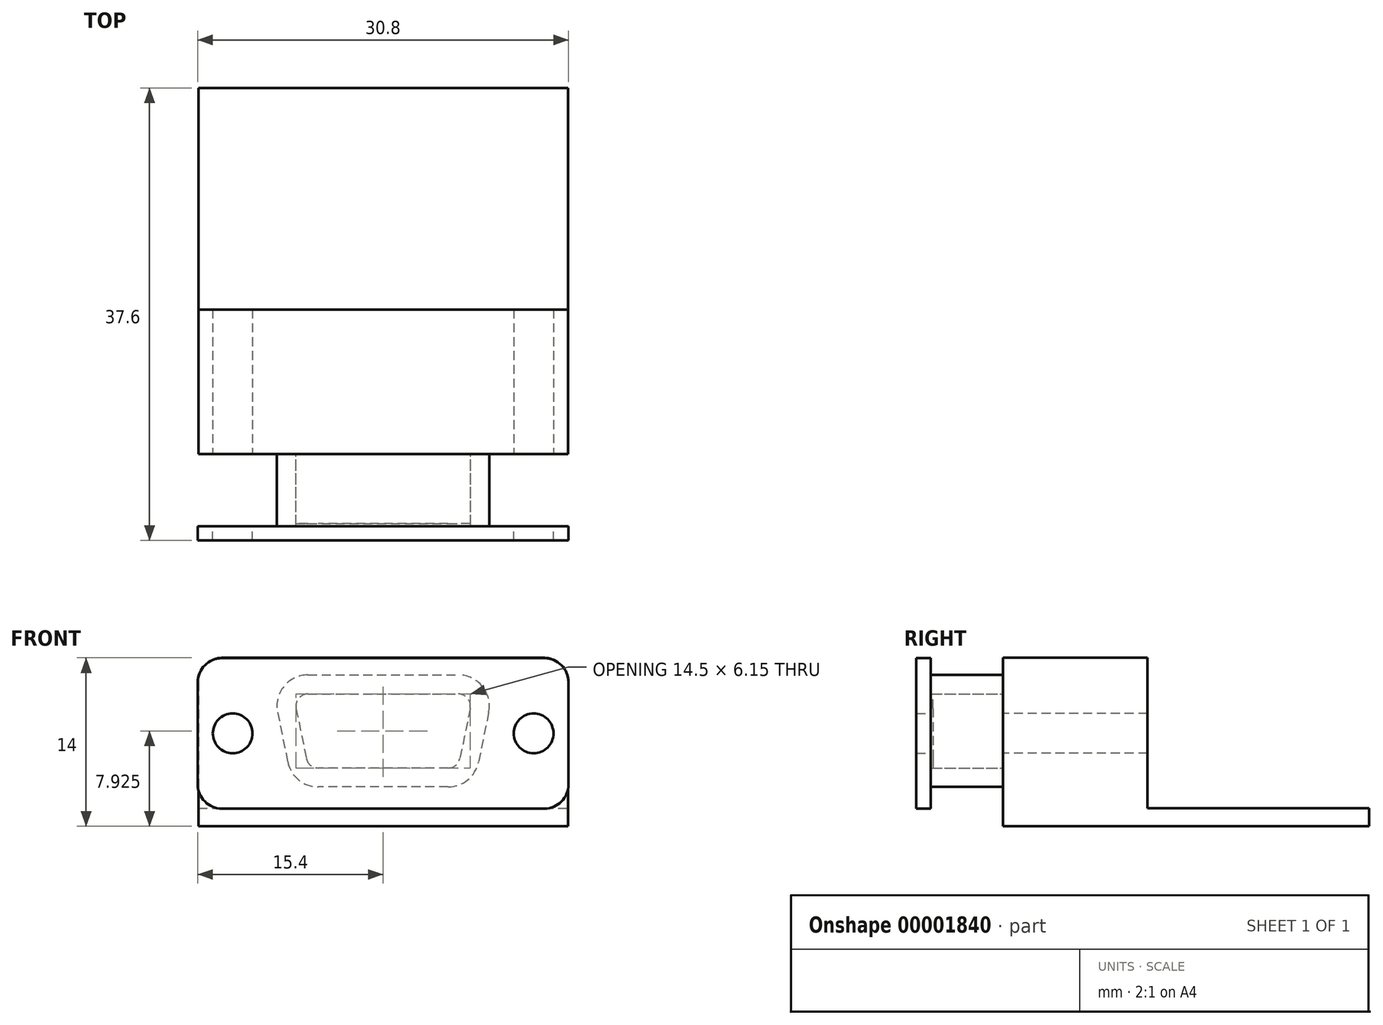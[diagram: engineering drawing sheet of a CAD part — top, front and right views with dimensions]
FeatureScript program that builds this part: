
annotation { "Feature Type Name" : "Feature", "Feature Type Description" : "" }
export const myFeature = defineFeature(function(context is Context, id is Id, definition is map)
    precondition{}
    {
        {
            var Q0;
            Q0=qCreatedBy(makeId("Front.planeOp"),FACE);
            var sketch = newSketch(context, id + "F0", { "sketchPlane" : qUnion([Q0])});
            skLineSegment(sketch, "E0.bottom", {"start": v(-13.35, 14) * mm, "end": v(13.35, 14) * mm});
            skLineSegment(sketch, "E0.top", {"start": v(-15.35, 0) * mm, "end": v(15.35, 0) * mm});
            skLineSegment(sketch, "E0.left", {"start": v(-15.35, 12) * mm, "end": v(-15.35, 0) * mm});
            skLineSegment(sketch, "E0.right", {"start": v(15.35, 12) * mm, "end": v(15.35, 0) * mm});
            skPoint(sketch, "E0.middle", {"position": v(0, 7) * mm});
            skLineSegment(sketch, "E1", {"start": v(-6.25, 11) * mm, "end": v(6.25, 11) * mm});
            skLineSegment(sketch, "E2", {"start": v(7.23, 9.8) * mm, "end": v(6.38, 5.65) * mm});
            skLineSegment(sketch, "E3", {"start": v(5.4, 4.85) * mm, "end": v(-5.4, 4.85) * mm});
            skLineSegment(sketch, "E4", {"start": v(0, 0) * mm, "end": v(0, 7) * mm, "construction": true});
            skLineSegment(sketch, "E5.MirrorCS", {"start": v(-7.23, 9.8) * mm, "end": v(-6.38, 5.65) * mm});
            skPoint(sketch, "E6.visualSharp", {"position": v(-7.48, 11) * mm});
            skArc(sketch, "E6.filletArc", {"start": v(-6.25, 11) * mm, "mid": v(-7.02, 10.63) * mm, "end": v(-7.23, 9.8) * mm});
            skPoint(sketch, "E7.visualSharp", {"position": v(-6.22, 4.85) * mm});
            skArc(sketch, "E7.filletArc", {"start": v(-6.38, 5.65) * mm, "mid": v(-6.03, 5.08) * mm, "end": v(-5.4, 4.85) * mm});
            skPoint(sketch, "E8.visualSharp", {"position": v(6.22, 4.85) * mm});
            skArc(sketch, "E8.filletArc", {"start": v(5.4, 4.85) * mm, "mid": v(6.03, 5.08) * mm, "end": v(6.38, 5.65) * mm});
            skPoint(sketch, "E9.visualSharp", {"position": v(7.48, 11) * mm});
            skArc(sketch, "E9.filletArc", {"start": v(7.23, 9.8) * mm, "mid": v(7.02, 10.63) * mm, "end": v(6.25, 11) * mm});
            skLineSegment(sketch, "E10", {"start": v(-15.35, 1.5) * mm, "end": v(15.35, 1.5) * mm});
            skPoint(sketch, "E11.visualSharp", {"position": v(-15.35, 14) * mm});
            skArc(sketch, "E11.filletArc", {"start": v(-13.35, 14) * mm, "mid": v(-14.76, 13.41) * mm, "end": v(-15.35, 12) * mm});
            skPoint(sketch, "E12.visualSharp", {"position": v(15.35, 14) * mm});
            skArc(sketch, "E12.filletArc", {"start": v(15.35, 12) * mm, "mid": v(14.76, 13.41) * mm, "end": v(13.35, 14) * mm});
            skLineSegment(sketch, "E13", {"start": v(-12.5, 7.72) * mm, "end": v(12.5, 7.72) * mm, "construction": true});
            skLineSegment(sketch, "E14", {"start": v(0, 7) * mm, "end": v(0, 7.72) * mm, "construction": true});
            skPoint(sketch, "E15", {"position": v(-6.8, 7.72) * mm});
            skCircle(sketch, "E16", {"center": v(-12.5, 7.72) * mm, "radius": 1.65 * mm});
            skCircle(sketch, "E17", {"center": v(12.5, 7.72) * mm, "radius": 1.65 * mm});
            skSolve(sketch);
        }
        {
            var Q0;
            {var subQ0=sQuery(id+"F0.wireOp",EDGE,"E0.top");Q0=makeQuery(id+"F0.imprint","IMPRINT",FACE,{"disambiguationData":[TD([[makeQuery(id+"F0.imprint","IMPRINT",EDGE,{"derivedFrom":subQ0}),1.0]])]});}
            extrude(context, id + "F1", {"entities" : qUnion([Q0]), "oppositeDirection" : true, "depth" : 30.4 * mm});
        }
        {
            var Q0;
            Q0=makeQuery(id+"F0.imprint","IMPRINT",FACE,{"disambiguationData":[TD([[makeQuery(id+"F0.imprint","IMPRINT",EDGE,{"derivedFrom":sQuery(id+"F0.wireOp",EDGE,"E0.bottom")}),-1.0]])]});
            var Q1;
            Q1=makeQuery(id+"F0.imprint","IMPRINT",FACE,{"disambiguationData":[TD([[makeQuery(id+"F0.imprint","IMPRINT",EDGE,{"derivedFrom":sQuery(id+"F0.wireOp",EDGE,"E1")}),-1.0]])]});
            extrude(context, id + "F2", {"entities" : qUnion([Q0, Q1]), "operationType" : NewBodyOperationType.ADD, "oppositeDirection" : true, "depth" : 12 * mm});
        }
        {
            var Q0;
            Q0=makeQuery(id+"F0.imprint","IMPRINT",FACE,{"disambiguationData":[TD([[makeQuery(id+"F0.imprint","IMPRINT",EDGE,{"derivedFrom":sQuery(id+"F0.wireOp",EDGE,"E1")}),-1.0]])]});
            extrude(context, id + "F3", {"entities" : qUnion([Q0]), "operationType" : NewBodyOperationType.ADD, "depth" : 5.8 * mm});
        }
        {
            var Q0;
            Q0=makeQuery(id+"F0.imprint","IMPRINT",FACE,{"disambiguationData":[TD([[makeQuery(id+"F0.imprint","IMPRINT",EDGE,{"derivedFrom":sQuery(id+"F0.wireOp",EDGE,"E0.bottom")}),-1.0]])]});
            var sketch = newSketch(context, id + "F4", { "sketchPlane" : qUnion([Q0])});
            skArc(sketch, "E18.0", {"start": v(-6.25, 12.58) * mm, "mid": v(-8.25, 11.63) * mm, "end": v(-8.77, 9.48) * mm});
            skLineSegment(sketch, "E18.1", {"start": v(-8.77, 9.48) * mm, "end": v(-7.92, 5.33) * mm});
            skLineSegment(sketch, "E18.2", {"start": v(-6.25, 12.58) * mm, "end": v(6.25, 12.58) * mm});
            skArc(sketch, "E18.3", {"start": v(-7.92, 5.33) * mm, "mid": v(-7.03, 3.85) * mm, "end": v(-5.4, 3.27) * mm});
            skArc(sketch, "E18.4", {"start": v(8.77, 9.48) * mm, "mid": v(8.25, 11.63) * mm, "end": v(6.25, 12.58) * mm});
            skLineSegment(sketch, "E18.5", {"start": v(8.77, 9.48) * mm, "end": v(7.92, 5.33) * mm});
            skArc(sketch, "E18.6", {"start": v(5.4, 3.28) * mm, "mid": v(7.03, 3.85) * mm, "end": v(7.92, 5.33) * mm});
            skLineSegment(sketch, "E18.7", {"start": v(5.4, 3.28) * mm, "end": v(-5.4, 3.28) * mm});
            skSolve(sketch);
        }
        {
            var Q0;
            Q0=makeQuery(id+"F4.imprint","IMPRINT",FACE,{"disambiguationData":[TD([[makeQuery(id+"F4.imprint","IMPRINT",EDGE,{"derivedFrom":sQuery(id+"F4.wireOp",EDGE,"E18.0")}),1.0]])]});
            extrude(context, id + "F5", {"entities" : qUnion([Q0]), "depth" : 6 * mm});
        }
        {
            var Q0;
            Q0=makeQuery(id+"F5.opExtrude","CAP_FACE",FACE,{"disambiguationData":[OSD([sQuery(id+"F0.wireOp",EDGE,"E1"),sQuery(id+"F0.wireOp",EDGE,"E2"),sQuery(id+"F0.wireOp",EDGE,"E3"),sQuery(id+"F0.wireOp",EDGE,"E5.MirrorCS"),sQuery(id+"F0.wireOp",EDGE,"E6.filletArc"),sQuery(id+"F0.wireOp",EDGE,"E7.filletArc"),sQuery(id+"F0.wireOp",EDGE,"E8.filletArc"),sQuery(id+"F0.wireOp",EDGE,"E9.filletArc"),sQuery(id+"F4.wireOp",EDGE,"E18.0"),sQuery(id+"F4.wireOp",EDGE,"E18.1"),sQuery(id+"F4.wireOp",EDGE,"E18.2"),sQuery(id+"F4.wireOp",EDGE,"E18.3"),sQuery(id+"F4.wireOp",EDGE,"E18.4"),sQuery(id+"F4.wireOp",EDGE,"E18.5"),sQuery(id+"F4.wireOp",EDGE,"E18.6"),sQuery(id+"F4.wireOp",EDGE,"E18.7")])],"isStart":false});
            var sketch = newSketch(context, id + "F6", { "sketchPlane" : qUnion([Q0])});
            skLineSegment(sketch, "E19.bottom", {"start": v(-13.4, 13.97) * mm, "end": v(13.4, 13.97) * mm});
            skLineSegment(sketch, "E19.top", {"start": v(-13.4, 1.47) * mm, "end": v(13.4, 1.47) * mm});
            skLineSegment(sketch, "E19.left", {"start": v(-15.4, 11.97) * mm, "end": v(-15.4, 3.47) * mm});
            skLineSegment(sketch, "E19.right", {"start": v(15.4, 11.97) * mm, "end": v(15.4, 3.47) * mm});
            skPoint(sketch, "E19.middle", {"position": v(0, 7.72) * mm});
            skCircle(sketch, "E20.0", {"center": v(-12.5, 7.72) * mm, "radius": 1.65 * mm});
            skCircle(sketch, "E20.1", {"center": v(12.5, 7.72) * mm, "radius": 1.65 * mm});
            skPoint(sketch, "E21.visualSharp", {"position": v(-15.4, 13.97) * mm});
            skArc(sketch, "E21.filletArc", {"start": v(-13.4, 13.97) * mm, "mid": v(-14.81, 13.39) * mm, "end": v(-15.4, 11.97) * mm});
            skPoint(sketch, "E22.visualSharp", {"position": v(15.4, 13.97) * mm});
            skArc(sketch, "E22.filletArc", {"start": v(15.4, 11.97) * mm, "mid": v(14.81, 13.39) * mm, "end": v(13.4, 13.97) * mm});
            skPoint(sketch, "E23.visualSharp", {"position": v(-15.4, 1.47) * mm});
            skArc(sketch, "E23.filletArc", {"start": v(-15.4, 3.47) * mm, "mid": v(-14.81, 2.06) * mm, "end": v(-13.4, 1.47) * mm});
            skPoint(sketch, "E24.visualSharp", {"position": v(15.4, 1.47) * mm});
            skArc(sketch, "E24.filletArc", {"start": v(13.4, 1.47) * mm, "mid": v(14.81, 2.06) * mm, "end": v(15.4, 3.47) * mm});
            skSolve(sketch);
        }
        {
            var Q0;
            Q0 = qSketchRegion(id + "F6", true);
            extrude(context, id + "F7", {"entities" : qUnion([Q0]), "operationType" : NewBodyOperationType.ADD, "depth" : 1.2 * mm});
        }
    });
